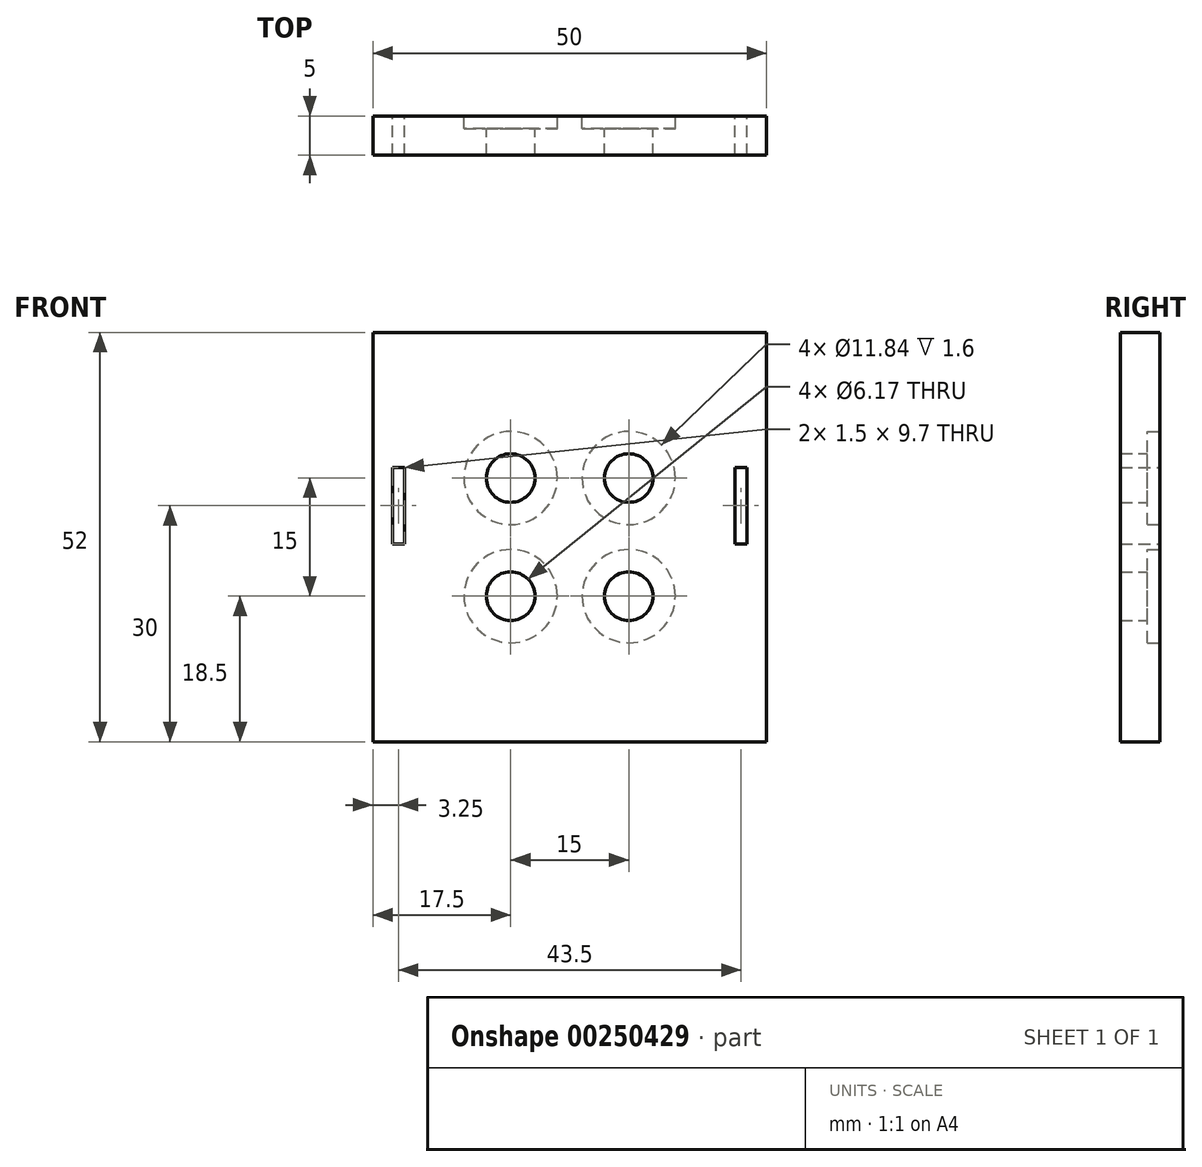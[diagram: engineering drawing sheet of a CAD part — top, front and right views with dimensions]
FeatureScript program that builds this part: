
annotation { "Feature Type Name" : "Feature", "Feature Type Description" : "" }
export const myFeature = defineFeature(function(context is Context, id is Id, definition is map)
    precondition{}
    {
        {
            var Q0;
            Q0=qCreatedBy(makeId("Front.planeOp"),FACE);
            var sketch = newSketch(context, id + "F0", { "sketchPlane" : qUnion([Q0])});
            skLineSegment(sketch, "E0.bottom", {"start": v(25, -26) * mm, "end": v(-25, -26) * mm});
            skLineSegment(sketch, "E0.top", {"start": v(25, 26) * mm, "end": v(-25, 26) * mm});
            skLineSegment(sketch, "E0.left", {"start": v(25, -26) * mm, "end": v(25, 26) * mm});
            skLineSegment(sketch, "E0.right", {"start": v(-25, -26) * mm, "end": v(-25, 26) * mm});
            skPoint(sketch, "E0.middle", {"position": v(0, 0) * mm});
            skLineSegment(sketch, "E1.bottom", {"start": v(-22.5, 8.85) * mm, "end": v(-21, 8.85) * mm});
            skLineSegment(sketch, "E1.top", {"start": v(-22.5, -0.85) * mm, "end": v(-21, -0.85) * mm});
            skLineSegment(sketch, "E1.left", {"start": v(-22.5, 8.85) * mm, "end": v(-22.5, -0.85) * mm});
            skLineSegment(sketch, "E1.right", {"start": v(-21, 8.85) * mm, "end": v(-21, -0.85) * mm});
            skLineSegment(sketch, "E2.bottom", {"start": v(21, 8.85) * mm, "end": v(22.5, 8.85) * mm});
            skLineSegment(sketch, "E2.top", {"start": v(21, -0.85) * mm, "end": v(22.5, -0.85) * mm});
            skLineSegment(sketch, "E2.left", {"start": v(21, 8.85) * mm, "end": v(21, -0.85) * mm});
            skLineSegment(sketch, "E2.right", {"start": v(22.5, 8.85) * mm, "end": v(22.5, -0.85) * mm});
            skSolve(sketch);
        }
        {
            var Q0;
            Q0 = qSketchRegion(id + "F0", true);
            extrude(context, id + "F1", {"entities" : qUnion([Q0]), "depth" : 5 * mm});
        }
        {
            var Q0;
            Q0=qCreatedBy(makeId("Front.planeOp"),FACE);
            var sketch = newSketch(context, id + "F2", { "sketchPlane" : qUnion([Q0])});
            skCircle(sketch, "E3", {"center": v(7.5, 7.5) * mm, "radius": 5.92 * mm});
            skCircle(sketch, "E4", {"center": v(7.5, -7.5) * mm, "radius": 5.92 * mm});
            skCircle(sketch, "E5", {"center": v(-7.5, -7.5) * mm, "radius": 5.92 * mm});
            skCircle(sketch, "E6", {"center": v(-7.5, 7.5) * mm, "radius": 5.92 * mm});
            skSolve(sketch);
        }
        {
            var Q0;
            Q0 = qSketchRegion(id + "F2", true);
            extrude(context, id + "F3", {"entities" : qUnion([Q0]), "operationType" : NewBodyOperationType.REMOVE, "depth" : 1.6 * mm});
        }
        {
            var Q0;
            Q0=qCreatedBy(makeId("Front.planeOp"),FACE);
            var sketch = newSketch(context, id + "F4", { "sketchPlane" : qUnion([Q0])});
            skCircle(sketch, "E7", {"center": v(7.5, 7.5) * mm, "radius": 3.09 * mm});
            skCircle(sketch, "E8", {"center": v(-7.5, 7.5) * mm, "radius": 3.09 * mm});
            skCircle(sketch, "E9", {"center": v(-7.5, -7.5) * mm, "radius": 3.09 * mm});
            skCircle(sketch, "E10", {"center": v(7.5, -7.5) * mm, "radius": 3.09 * mm});
            skSolve(sketch);
        }
        {
            var Q0;
            Q0 = qSketchRegion(id + "F4", true);
            extrude(context, id + "F5", {"entities" : qUnion([Q0]), "operationType" : NewBodyOperationType.REMOVE, "endBound" : BoundingType.THROUGH_ALL, "depth" : 25 * mm});
        }
    });
